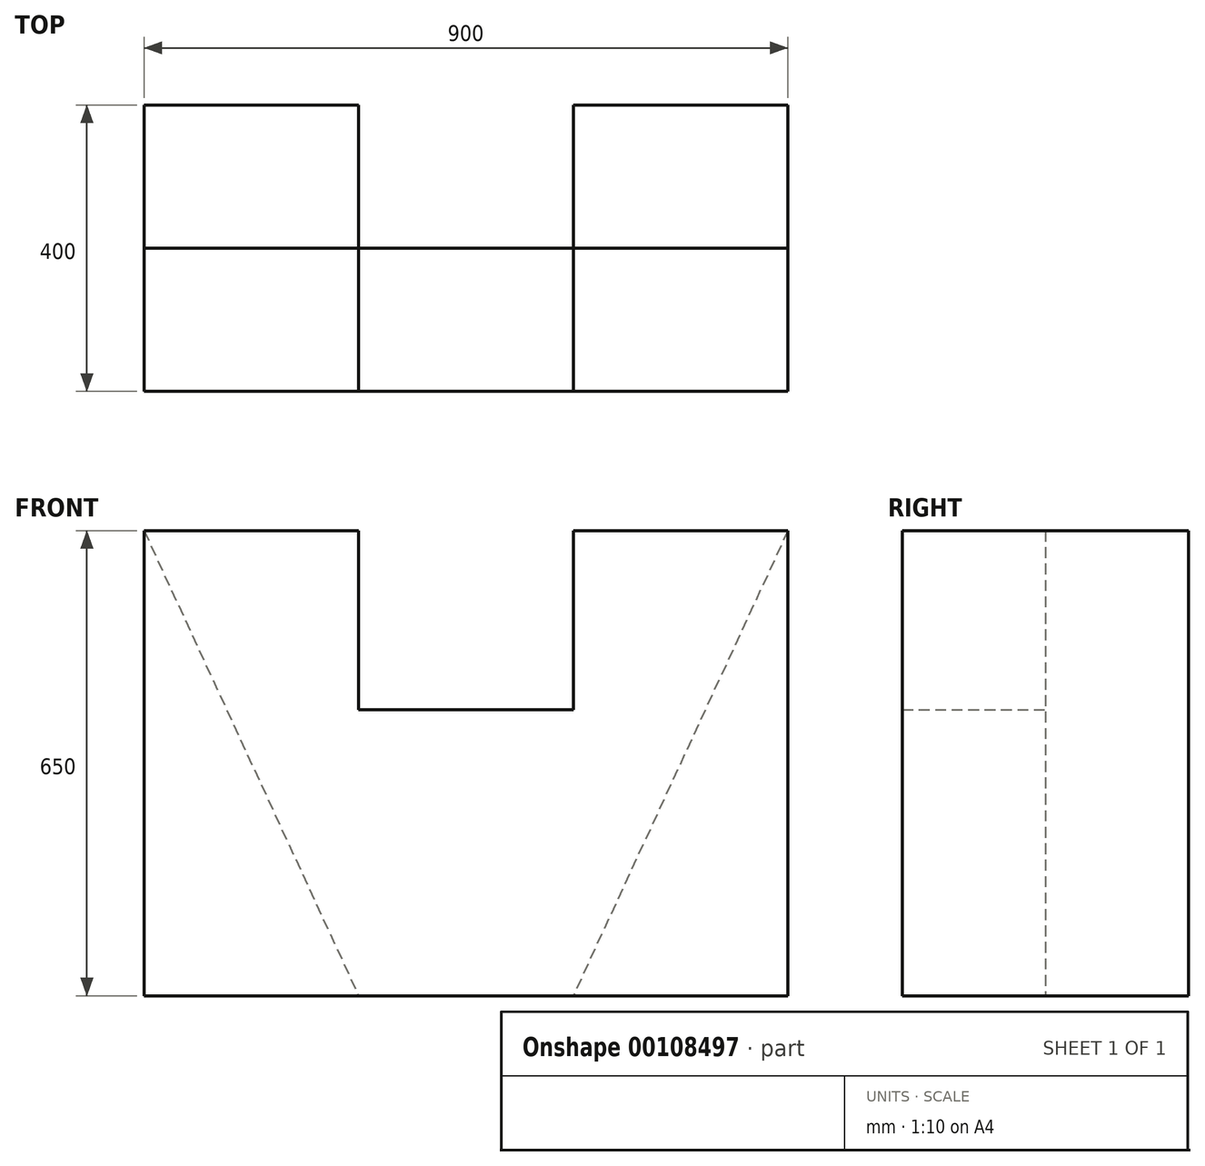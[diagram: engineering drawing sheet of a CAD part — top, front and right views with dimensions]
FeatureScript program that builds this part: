
annotation { "Feature Type Name" : "Feature", "Feature Type Description" : "" }
export const myFeature = defineFeature(function(context is Context, id is Id, definition is map)
    precondition{}
    {
        {
            var Q0;
            Q0=qCreatedBy(makeId("Front.planeOp"),FACE);
            var sketch = newSketch(context, id + "F0", { "sketchPlane" : qUnion([Q0])});
            skLineSegment(sketch, "E0.bottom", {"start": v(-450, 325) * mm, "end": v(-150, 325) * mm});
            skLineSegment(sketch, "E0.top", {"start": v(-450, -325) * mm, "end": v(450, -325) * mm});
            skLineSegment(sketch, "E0.left", {"start": v(-450, 325) * mm, "end": v(-450, -325) * mm});
            skLineSegment(sketch, "E0.right", {"start": v(450, 325) * mm, "end": v(450, -325) * mm});
            skPoint(sketch, "E0.middle", {"position": v(0, 0) * mm});
            skLineSegment(sketch, "E1.top", {"start": v(-150, 75) * mm, "end": v(150, 75) * mm});
            skLineSegment(sketch, "E1.left", {"start": v(-150, 325) * mm, "end": v(-150, 75) * mm});
            skLineSegment(sketch, "E1.right", {"start": v(150, 325) * mm, "end": v(150, 75) * mm});
            skPoint(sketch, "E1.middle", {"position": v(0, 325) * mm});
            skPoint(sketch, "E1.bottom.start.orphan", {"position": v(-150, 575) * mm});
            skPoint(sketch, "E2.orphan", {"position": v(150, 575) * mm});
            skLineSegment(sketch, "E3.trimOffspring", {"start": v(150, 325) * mm, "end": v(450, 325) * mm});
            skSolve(sketch);
        }
        {
            var Q0;
            Q0 = qSketchRegion(id + "F0", true);
            extrude(context, id + "F1", {"entities" : qUnion([Q0]), "depth" : 200 * mm});
        }
        {
            var Q0;
            Q0=makeQuery(id+"F1.opExtrude","CAP_FACE",FACE,{"disambiguationData":[OSD([sQuery(id+"F0.wireOp",EDGE,"E0.bottom"),sQuery(id+"F0.wireOp",EDGE,"E0.top"),sQuery(id+"F0.wireOp",EDGE,"E0.left"),sQuery(id+"F0.wireOp",EDGE,"E0.right"),sQuery(id+"F0.wireOp",EDGE,"E1.top"),sQuery(id+"F0.wireOp",EDGE,"E1.left"),sQuery(id+"F0.wireOp",EDGE,"E1.right"),sQuery(id+"F0.wireOp",EDGE,"E3.trimOffspring")])],"isStart":true});
            var sketch = newSketch(context, id + "F2", { "sketchPlane" : qUnion([Q0])});
            skLineSegment(sketch, "E4", {"start": v(450, 325) * mm, "end": v(150, -325) * mm});
            skLineSegment(sketch, "E5", {"start": v(150, -325) * mm, "end": v(450, -325) * mm});
            skLineSegment(sketch, "E6", {"start": v(450, -325) * mm, "end": v(450, 325) * mm});
            skLineSegment(sketch, "E7", {"start": v(-450, 325) * mm, "end": v(-150, -325) * mm});
            skLineSegment(sketch, "E8", {"start": v(-150, -325) * mm, "end": v(-450, -325) * mm});
            skLineSegment(sketch, "E9", {"start": v(-450, -325) * mm, "end": v(-450, 325) * mm});
            skSolve(sketch);
        }
        {
            var Q0;
            Q0 = qSketchRegion(id + "F2", true);
            extrude(context, id + "F3", {"entities" : qUnion([Q0]), "operationType" : NewBodyOperationType.ADD, "depth" : 200 * mm});
        }
    });
